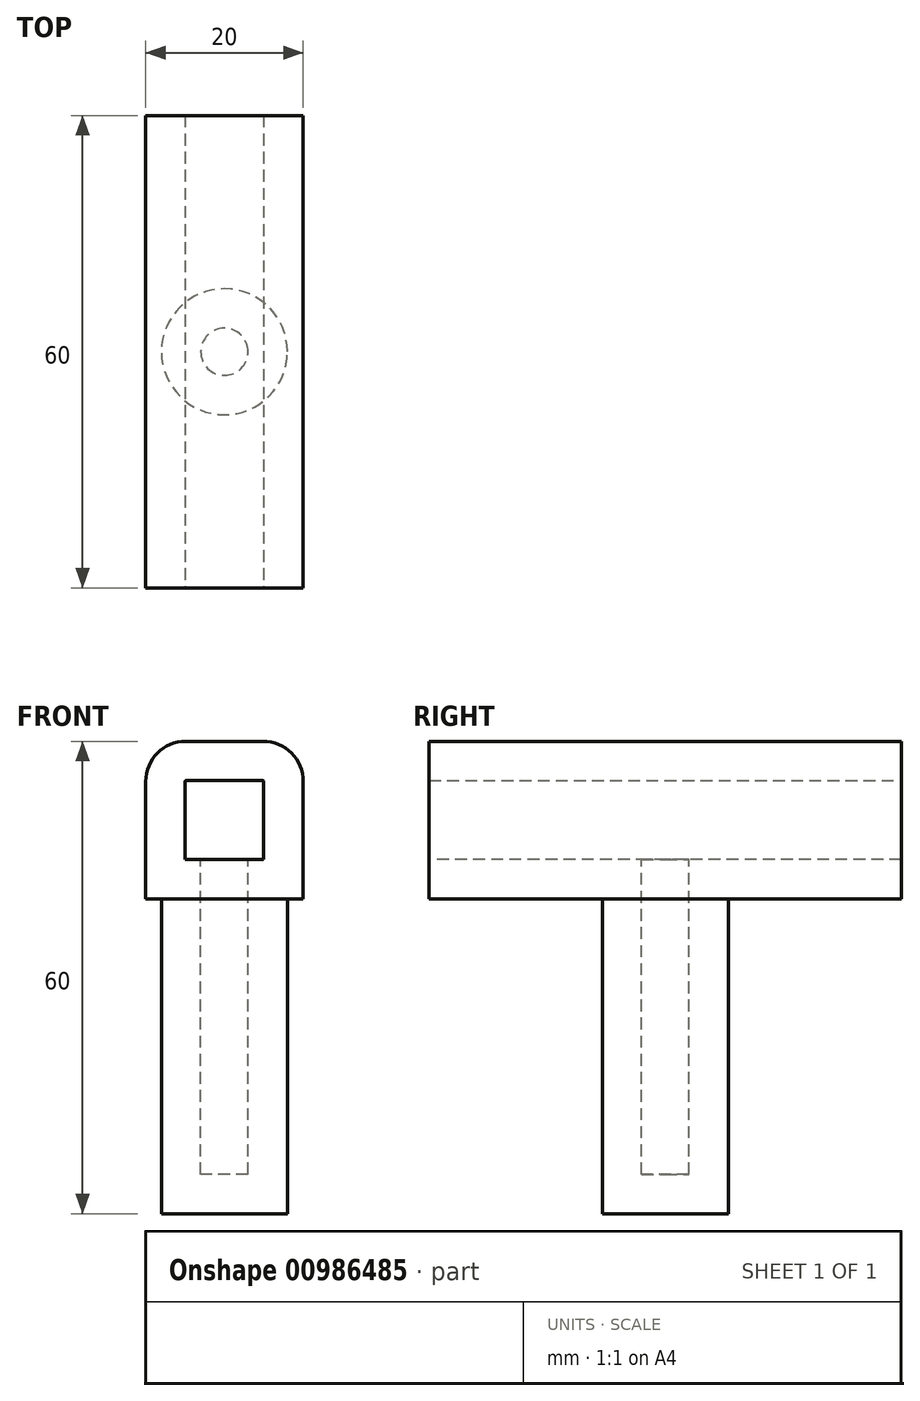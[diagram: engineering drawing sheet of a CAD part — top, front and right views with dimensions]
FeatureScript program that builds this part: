
annotation { "Feature Type Name" : "Feature", "Feature Type Description" : "" }
export const myFeature = defineFeature(function(context is Context, id is Id, definition is map)
    precondition{}
    {
        {
            var Q0;
            Q0=qCreatedBy(makeId("Top.planeOp"),FACE);
            var sketch = newSketch(context, id + "F0", { "sketchPlane" : qUnion([Q0])});
            skCircle(sketch, "E0", {"center": v(0, 0) * mm, "radius": 8 * mm});
            skSolve(sketch);
        }
        {
            var Q0;
            Q0 = qSketchRegion(id + "F0", true);
            extrude(context, id + "F1", {"entities" : qUnion([Q0]), "oppositeDirection" : true, "depth" : 40 * mm, "offsetDistance" : 25.4 * mm});
        }
        {
            var Q0;
            Q0=qCreatedBy(makeId("Top.planeOp"),FACE);
            var sketch = newSketch(context, id + "F2", { "sketchPlane" : qUnion([Q0])});
            skLineSegment(sketch, "E1.bottom", {"start": v(10, 30) * mm, "end": v(-10, 30) * mm});
            skLineSegment(sketch, "E1.top", {"start": v(10, -30) * mm, "end": v(-10, -30) * mm});
            skLineSegment(sketch, "E1.left", {"start": v(10, 30) * mm, "end": v(10, -30) * mm});
            skLineSegment(sketch, "E1.right", {"start": v(-10, 30) * mm, "end": v(-10, -30) * mm});
            skPoint(sketch, "E1.middle", {"position": v(0, 0) * mm});
            skSolve(sketch);
        }
        {
            var Q0;
            Q0 = qSketchRegion(id + "F2", true);
            var Q1;
            Q1 = qSketchRegion(id + "F0", true);
            extrude(context, id + "F3", {"entities" : qUnion([Q0, Q1]), "operationType" : NewBodyOperationType.ADD, "depth" : 20 * mm, "offsetDistance" : 25.4 * mm});
        }
        {
            var Q0;
            Q0=makeQuery(id+"F3.opExtrude","CAP_EDGE",EDGE,{"disambiguationData":[OSD([sQuery(id+"F2.wireOp",EDGE,"E1.right")])],"isStart":false});
            var Q1;
            Q1=makeQuery(id+"F3.opExtrude","CAP_EDGE",EDGE,{"disambiguationData":[OSD([sQuery(id+"F2.wireOp",EDGE,"E1.left")])],"isStart":false});
            fillet(context, id + "F4", {"entities" : qUnion([Q0, Q1]), "radius" : 5.08 * mm, "tangentPropagation" : true, "allowEdgeOverflow" : false});
        }
        {
            var Q0;
            Q0=makeQuery(id+"F3.opExtrude","SWEPT_FACE",FACE,{"disambiguationData":[OSD([sQuery(id+"F2.wireOp",EDGE,"E1.top")])]});
            var sketch = newSketch(context, id + "F5", { "sketchPlane" : qUnion([Q0])});
            skSolve(sketch);
        }
        {
            var Q0;
            Q0=makeQuery(id+"F3.opExtrude","SWEPT_FACE",FACE,{"disambiguationData":[OSD([sQuery(id+"F2.wireOp",EDGE,"E1.top")])]});
            var Q1;
            Q1=makeQuery(id+"F3.opExtrude","SWEPT_FACE",FACE,{"disambiguationData":[OSD([sQuery(id+"F2.wireOp",EDGE,"E1.bottom")])]});
            shell(context, id + "F6", {"entities" : qUnion([Q0, Q1]), "thickness" : 5 * mm});
        }
    });
